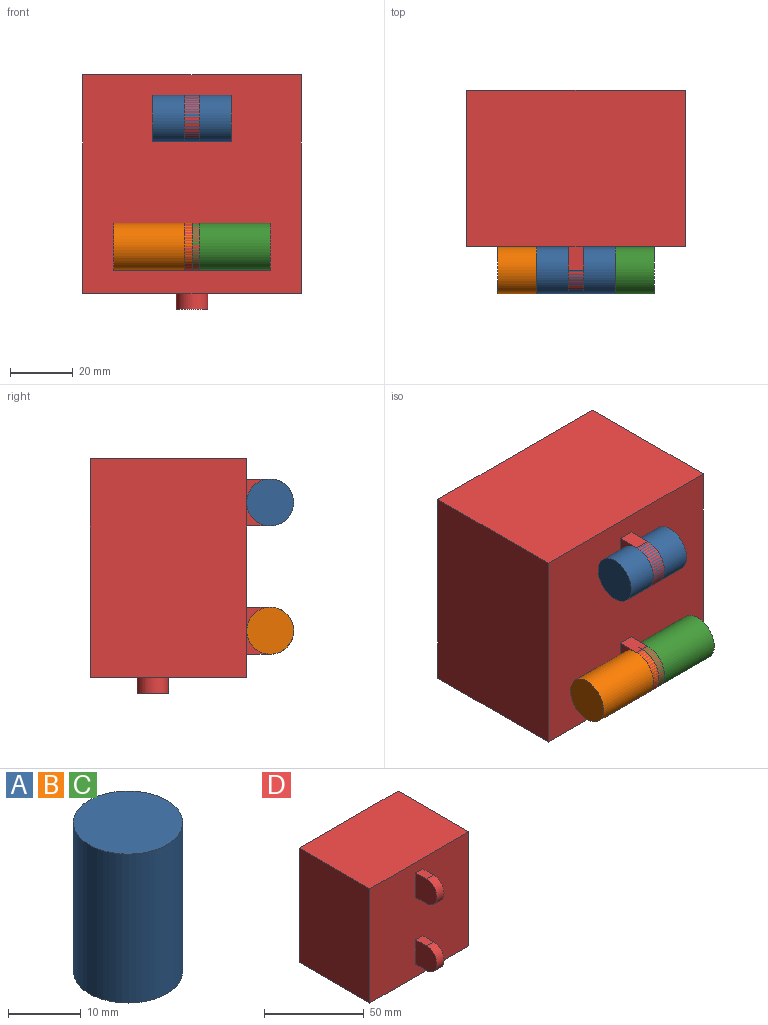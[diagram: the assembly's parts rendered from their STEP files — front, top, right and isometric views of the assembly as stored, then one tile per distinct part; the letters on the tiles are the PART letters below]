
ASSEMBLY  parts=4 mates=6
PART A: 3 faces, bbox 15x15x25 mm
  f0: cylinder r=7.5mm len=25mm, axis (0,0,-1), area 1178.1mm2, adj f1,f2
  f1: plane 15x15mm, normal (0,0,1), area 176.7mm2, adj f0
  f2: plane 15x15mm, normal (0,0,-1), area 176.7mm2, adj f0
PART B: same geometry as A
PART C: same geometry as A
PART D: 18 faces, bbox 70x65x75 mm
  f0: plane 70x70mm, normal (0,-1,0), area 4750mm2, adj f1,f2,f3,f4,f8,f9,f11,f12
  f1: plane 70x50mm, normal (-1,0,0), area 3500mm2, adj f0,f2,f4,f5
  f2: plane 70x50mm, normal (0,0,-1), area 3421.5mm2, adj f0,f1,f3,f5,f6
  f3: plane 70x50mm, normal (1,0,0), area 3500mm2, adj f0,f2,f4,f5
  f4: plane 70x50mm, normal (0,0,1), area 3500mm2, adj f0,f1,f3,f5
  f5: plane 70x70mm, normal (0,1,0), area 4900mm2, adj f1,f2,f3,f4
  f6: cylinder r=5mm len=10mm, axis (0,0,1), area 157.1mm2, adj f2,f7
  f7: plane 10x10mm, normal (0,0,-1), area 78.5mm2, adj f6
  f8: plane 7.5x5mm, normal (0,0,-1), area 37.5mm2, adj f0,f10,f11,f12
  f9: plane 7.5x5mm, normal (0,0,1), area 37.5mm2, adj f0,f10,f11,f12
  f10: cylinder r=7.5mm len=15mm, axis (-1,0,0), area 117.8mm2, adj f8,f9,f11,f12
  f11: plane 15x15mm, normal (1,0,0), area 200.9mm2, adj f0,f8,f9,f10
  f12: plane 15x15mm, normal (-1,0,0), area 200.9mm2, adj f0,f8,f9,f10
  f13: plane 7.5x5mm, normal (0,0,-1), area 37.5mm2, adj f0,f15,f16,f17
  f14: plane 7.5x5mm, normal (0,0,1), area 37.5mm2, adj f0,f15,f16,f17
  f15: cylinder r=7.5mm len=15mm, axis (-1,0,0), area 117.8mm2, adj f13,f14,f16,f17
  f16: plane 15x15mm, normal (1,0,0), area 200.9mm2, adj f0,f13,f14,f15
  f17: plane 15x15mm, normal (-1,0,0), area 200.9mm2, adj f0,f13,f14,f15
PLACE A rot(axis=(-0.71,-0.01,0.71),179.1deg) t=(12.5,-57.5,56)mm
PLACE B rot(axis=(-0.71,0,-0.71),180deg) t=(-25,-57.5,15)mm
PLACE C rot(axis=(0,1,0),90deg) t=(0,-57.5,15)mm
PLACE D at identity fixed
MATE planar C.f0 <-> B.f0  axis (-1,0,0) through (0,-57.5,15)mm
MATE cylindrical A.f0 <-> D.f10  axis (1,0,0) through (0,-57.5,56)mm
MATE slider B.f0 <-> C.f0  axis (-1,0,0) through (-12.5,-57.5,15)mm
MATE planar A.f0 <-> B.f0  axis (1,0,0) through (0,-57.5,56)mm
MATE cylindrical B.f0 <-> D.f15  axis (-1,0,0) through (-12.5,-57.5,15)mm
MATE planar C.f0 <-> D.f15  axis (-1,0,0) through (0,-57.5,15)mm
